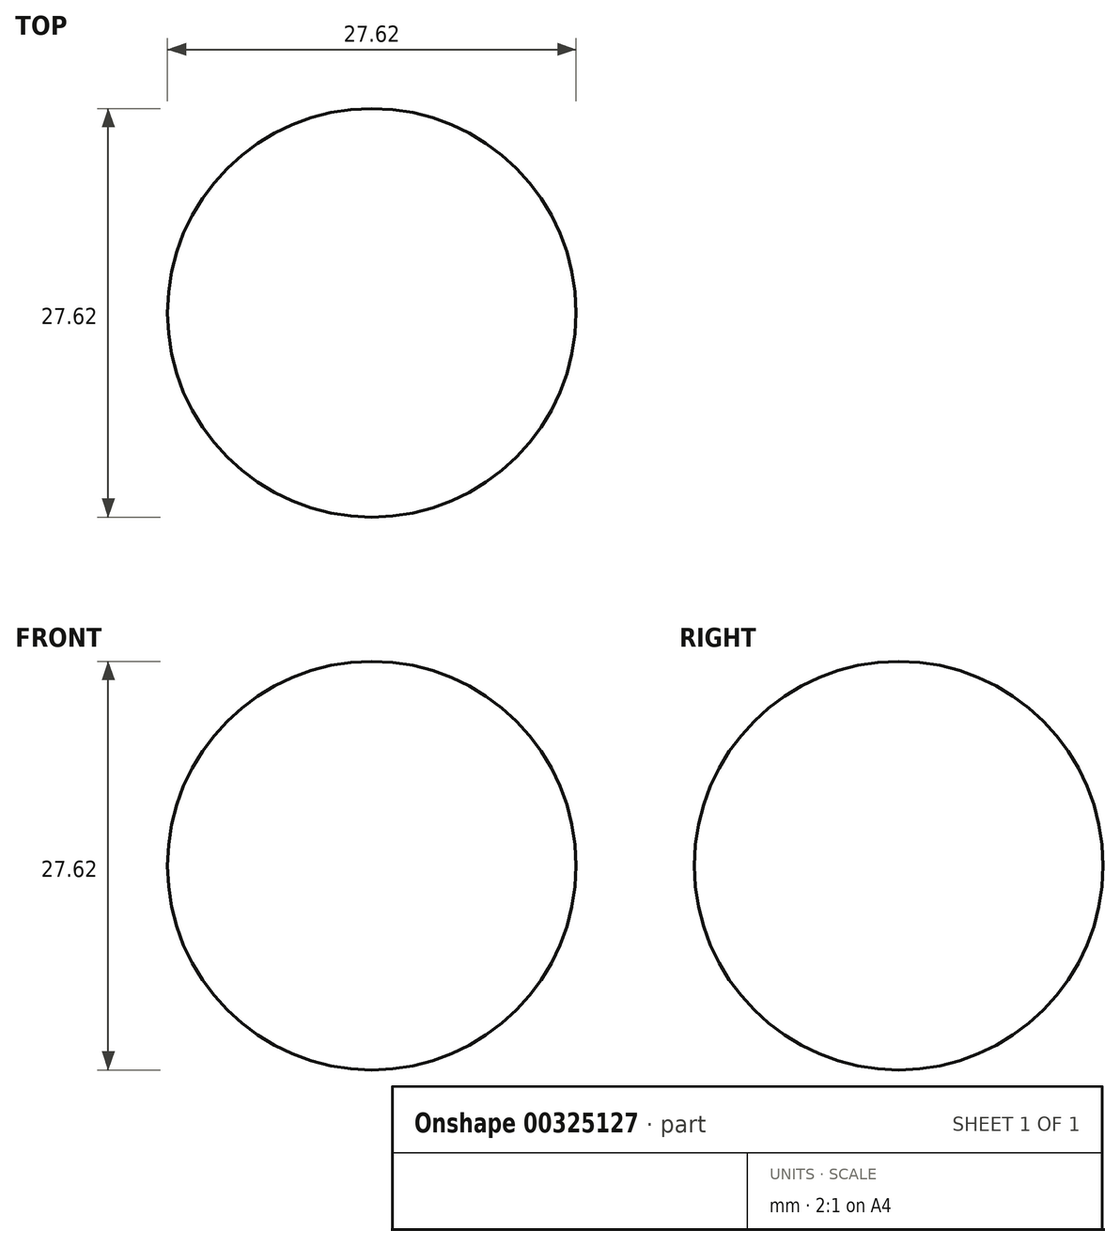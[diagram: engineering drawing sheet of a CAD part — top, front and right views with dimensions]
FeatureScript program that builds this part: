
annotation { "Feature Type Name" : "Feature", "Feature Type Description" : "" }
export const myFeature = defineFeature(function(context is Context, id is Id, definition is map)
    precondition{}
    {
        {
            var Q0;
            Q0=qCreatedBy(makeId("Top.planeOp"),FACE);
            var sketch = newSketch(context, id + "F0", { "sketchPlane" : qUnion([Q0])});
            skArc(sketch, "E0", {"start": v(0, 18.41) * mm, "mid": v(-18.41, 0) * mm, "end": v(0, -18.41) * mm});
            skLineSegment(sketch, "E1", {"start": v(0, 18.41) * mm, "end": v(0, -18.41) * mm});
            skSolve(sketch);
        }
        {
            var Q0;
            Q0=qCreatedBy(makeId("Top.planeOp"),FACE);
            var sketch = newSketch(context, id + "F1", { "sketchPlane" : qUnion([Q0])});
            skLineSegment(sketch, "E2", {"start": v(0, 0) * mm, "end": v(0, 36.24) * mm});
            skSolve(sketch);
        }
        {
            var Q0;
            Q0=makeQuery(id+"F0.imprint","IMPRINT",FACE,{"disambiguationData":[TD([[makeQuery(id+"F0.imprint","IMPRINT",EDGE,{"derivedFrom":sQuery(id+"F0.wireOp",EDGE,"E0")}),1.0]])]});
            var Q1;
            Q1=sQuery(id+"F1.wireOp",EDGE,"E2");
            revolve(context, id + "F2", {"entities" : qUnion([Q0]), "axis" : qUnion([Q1]), "revolveType" : RevolveType.FULL});
        }
        {
            var Q0;
            Q0=makeQuery(id+"F2.opRevolve","SWEPT_BODY",BODY,{"disambiguationData":[OSD([sQuery(id+"F0.wireOp",EDGE,"E0"),sQuery(id+"F0.wireOp",EDGE,"E1")])]});
            var Q1;
            Q1=qCreatedBy(makeId("Origin.pointOp"),VERTEX);
            transform(context, id + "F3", {"entities" : qUnion([Q0]), "transformType" : TransformType.SCALE_UNIFORMLY, "scale" : .75, "scalePoint" : qUnion([Q1]), "makeCopy" : false});
        }
    });
